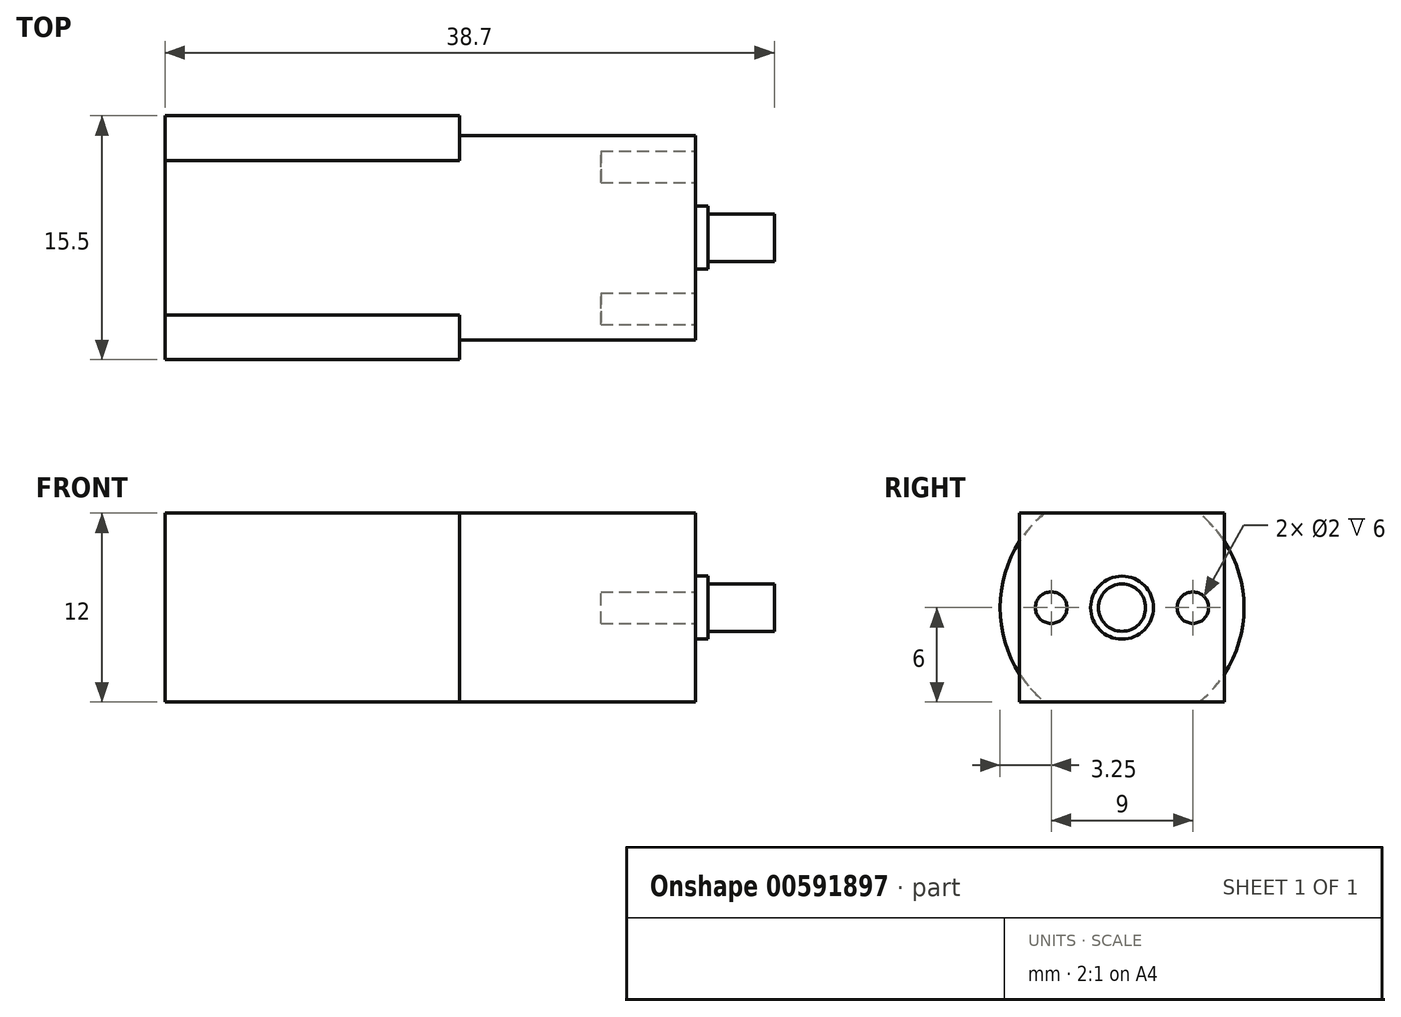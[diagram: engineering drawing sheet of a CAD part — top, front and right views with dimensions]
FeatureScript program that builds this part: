
annotation { "Feature Type Name" : "Feature", "Feature Type Description" : "" }
export const myFeature = defineFeature(function(context is Context, id is Id, definition is map)
    precondition{}
    {
        {
            var Q0;
            Q0=qCreatedBy(makeId("Right.planeOp"),FACE);
            var sketch = newSketch(context, id + "F0", { "sketchPlane" : qUnion([Q0])});
            skLineSegment(sketch, "E0", {"start": v(-4.9, 6) * mm, "end": v(4.9, 6) * mm});
            skLineSegment(sketch, "E1", {"start": v(-4.9, -6) * mm, "end": v(4.9, -6) * mm});
            skArc(sketch, "E2", {"start": v(4.9, 6) * mm, "mid": v(7.75, 0) * mm, "end": v(4.9, -6) * mm});
            skArc(sketch, "E3", {"start": v(-4.9, 6) * mm, "mid": v(-7.75, 0) * mm, "end": v(-4.9, -6) * mm});
            skLineSegment(sketch, "E4", {"start": v(-4.9, 6) * mm, "end": v(4.9, -6) * mm, "construction": true});
            skSolve(sketch);
        }
        {
            var Q0;
            Q0 = qSketchRegion(id + "F0", true);
            extrude(context, id + "F1", {"entities" : qUnion([Q0]), "depth" : 18.7 * mm, "offsetDistance" : 25 * mm});
        }
        {
            var Q0;
            Q0=makeQuery(id+"F1.opExtrude","CAP_FACE",FACE,{"disambiguationData":[OSD([sQuery(id+"F0.wireOp",EDGE,"E0"),sQuery(id+"F0.wireOp",EDGE,"E1"),sQuery(id+"F0.wireOp",EDGE,"E2"),sQuery(id+"F0.wireOp",EDGE,"E3")])],"isStart":false});
            var sketch = newSketch(context, id + "F2", { "sketchPlane" : qUnion([Q0])});
            skLineSegment(sketch, "E5.bottom", {"start": v(6.5, 6) * mm, "end": v(-6.5, 6) * mm});
            skLineSegment(sketch, "E5.top", {"start": v(6.5, -6) * mm, "end": v(-6.5, -6) * mm});
            skLineSegment(sketch, "E5.left", {"start": v(6.5, 6) * mm, "end": v(6.5, -6) * mm});
            skLineSegment(sketch, "E5.right", {"start": v(-6.5, 6) * mm, "end": v(-6.5, -6) * mm});
            skPoint(sketch, "E5.middle", {"position": v(0, 0) * mm});
            skSolve(sketch);
        }
        {
            var Q0;
            Q0 = qSketchRegion(id + "F2", true);
            extrude(context, id + "F3", {"entities" : qUnion([Q0]), "operationType" : NewBodyOperationType.ADD, "depth" : 15 * mm, "offsetDistance" : 25 * mm});
        }
        {
            var Q0;
            Q0=makeQuery(id+"F3.opExtrude","CAP_FACE",FACE,{"disambiguationData":[OSD([sQuery(id+"F2.wireOp",EDGE,"E5.bottom"),sQuery(id+"F2.wireOp",EDGE,"E5.top"),sQuery(id+"F2.wireOp",EDGE,"E5.left"),sQuery(id+"F2.wireOp",EDGE,"E5.right")])],"isStart":false});
            var sketch = newSketch(context, id + "F4", { "sketchPlane" : qUnion([Q0])});
            skCircle(sketch, "E6", {"center": v(0, 0) * mm, "radius": 1.5 * mm});
            skCircle(sketch, "E7", {"center": v(-4.5, 0) * mm, "radius": 1 * mm});
            skCircle(sketch, "E8", {"center": v(4.5, 0) * mm, "radius": 1 * mm});
            skLineSegment(sketch, "E9", {"start": v(-4.5, 0) * mm, "end": v(4.5, 0) * mm, "construction": true});
            skCircle(sketch, "E10", {"center": v(0, 0) * mm, "radius": 2 * mm});
            skSolve(sketch);
        }
        {
            var Q0;
            Q0=makeQuery(id+"F4.imprint","IMPRINT",FACE,{"disambiguationData":[TD([[makeQuery(id+"F4.imprint","IMPRINT",EDGE,{"derivedFrom":sQuery(id+"F4.wireOp",EDGE,"E6")}),1.0]])]});
            extrude(context, id + "F5", {"entities" : qUnion([Q0]), "operationType" : NewBodyOperationType.ADD, "depth" : 5 * mm, "offsetDistance" : 25 * mm});
        }
        {
            var Q0;
            Q0=makeQuery(id+"F4.imprint","IMPRINT",FACE,{"disambiguationData":[TD([[makeQuery(id+"F4.imprint","IMPRINT",EDGE,{"derivedFrom":sQuery(id+"F4.wireOp",EDGE,"E7")}),1.0]])]});
            var Q1;
            Q1=makeQuery(id+"F4.imprint","IMPRINT",FACE,{"disambiguationData":[TD([[makeQuery(id+"F4.imprint","IMPRINT",EDGE,{"derivedFrom":sQuery(id+"F4.wireOp",EDGE,"E8")}),1.0]])]});
            extrude(context, id + "F6", {"entities" : qUnion([Q0, Q1]), "operationType" : NewBodyOperationType.REMOVE, "oppositeDirection" : true, "depth" : 6 * mm, "offsetDistance" : 25 * mm});
        }
        {
            var Q0;
            Q0=makeQuery(id+"F4.imprint","IMPRINT",FACE,{"disambiguationData":[TD([[makeQuery(id+"F4.imprint","IMPRINT",EDGE,{"derivedFrom":sQuery(id+"F4.wireOp",EDGE,"E6")}),-1.0]])]});
            extrude(context, id + "F7", {"entities" : qUnion([Q0]), "operationType" : NewBodyOperationType.ADD, "depth" : 0.8 * mm, "offsetDistance" : 25 * mm});
        }
    });
